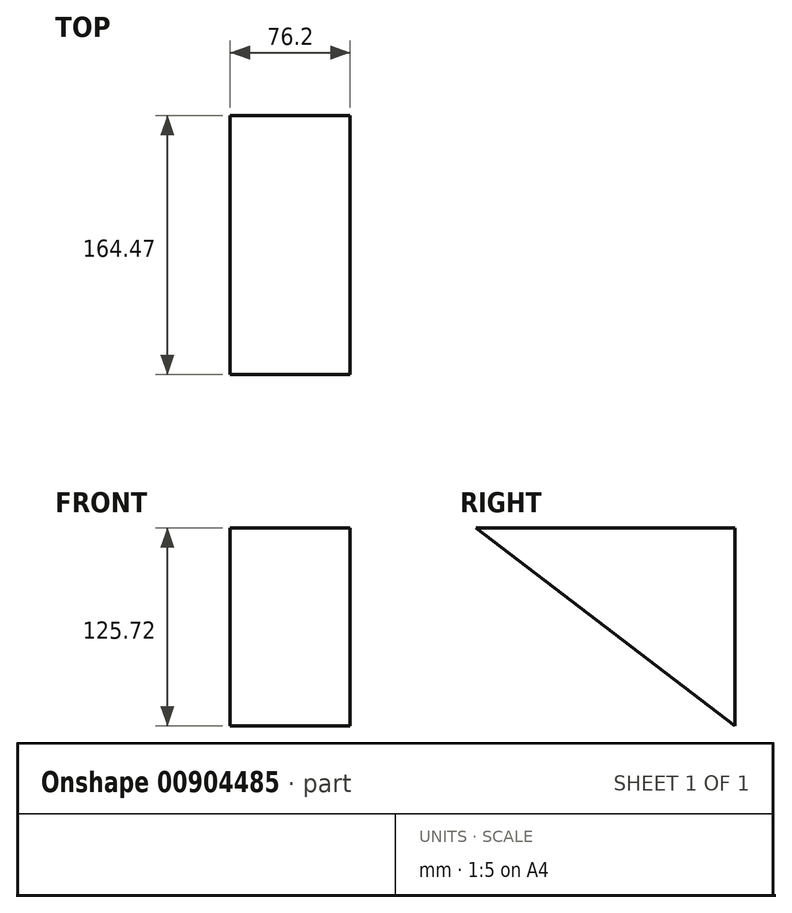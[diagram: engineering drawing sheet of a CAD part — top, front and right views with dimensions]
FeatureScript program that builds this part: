
annotation { "Feature Type Name" : "Feature", "Feature Type Description" : "" }
export const myFeature = defineFeature(function(context is Context, id is Id, definition is map)
    precondition{}
    {
        {
            var Q0;
            Q0=qCreatedBy(makeId("Right.planeOp"),FACE);
            var sketch = newSketch(context, id + "F0", { "sketchPlane" : qUnion([Q0])});
            skLineSegment(sketch, "E0", {"start": v(0, 0) * mm, "end": v(0, 125.72) * mm});
            skLineSegment(sketch, "E1", {"start": v(0, 125.72) * mm, "end": v(-164.47, 125.72) * mm});
            skLineSegment(sketch, "E2", {"start": v(-164.47, 125.72) * mm, "end": v(0, 0) * mm});
            skSolve(sketch);
        }
        {
            var Q0;
            Q0=makeQuery(id+"F0.imprint","IMPRINT",FACE,{"disambiguationData":[TD([[makeQuery(id+"F0.imprint","IMPRINT",EDGE,{"derivedFrom":sQuery(id+"F0.wireOp",EDGE,"E0")}),1.0]])]});
            extrude(context, id + "F1", {"entities" : qUnion([Q0]), "oppositeDirection" : true, "depth" : 76.2 * mm, "offsetDistance" : 25.4 * mm});
        }
    });
